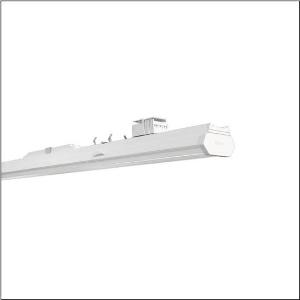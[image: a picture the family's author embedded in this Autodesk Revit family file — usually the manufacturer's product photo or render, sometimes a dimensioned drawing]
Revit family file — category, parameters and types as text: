
# Revit family: licross_11_protected_mo_51tp12dn695g
name_source: partatom
category: Lighting Fixtures
units: mm (PartAtom-declared; Revit-internal decimal feet)

## family parameters
Cut with Voids When Loaded = No
Host = Face
Light Source = No
Part Type = Normal
Room Calculation Point = No
Round Connector Dimension = Use Diameter
Shared = No

## types (1)
- --- (1 x LED, 9730 lm, 57.1 W, 6500K)
    Apparent Load = 57 VA
    CIE Flux Codes = 73 92 98 99 100
    Color Rendering = 80
    Color Temperature = 6500K
    Default Elevation = 1800 mm
    Description = Licross 11 Protected MO, luminaire insert, of sheet steel, galvanised, coil coated, white, length: 1.500mm, width: 90mm, height: 101mm, LED rated luminous flux: 9.730lm, light colour: 865, SDCM (Standard Deviation of Colour Matching)MacAdam ≤ 2 SDCM (initial), control gear: DALI 2, with plug, 5-pole, with phase selection, mains connection: 220..240V, AC, 50/60Hz, rated input power: 57W, internal wiring halogen-free, primary optical cover: cover, of PMMA, light emission: direct distribution, primary light characteristic: symmetric, protection rating (complete): IP64, insulation class (complete): insulation class I (protective earthing), certification: CE, ENEC, VDE, UKCA, protection symbol: D if used in an environment with conductive dust loads with corresponding accessories, impact resistance: IK06, permissible ambient temperature for indoor applications: -25..+35°C, corresponds to IFS (International Featured Standards) requirements for safety and quality in the food industry, reducing of maximum allowable ambient temperature of 5°C with ceiling mounting, LABS conformity tested according to VDMA 24364:2018-05, The light source and the operating device comply with the requirements of the Ecodesign Regulation (EU) 2019/2020 and are replaceable in accordance with this regulation, packaging unit: 1 piece
    Height = 92 mm
    Lamp = 1 x LED
    Lamp Light Flux = 9730 lm
    Lamp Power = 57.1 W
    Lamp count = 1
    Length = 1500 mm
    Luminous efficacy = 170 lm/W
    Manufacturer = Siteco
    ModVariant = No
    Model = 51TP12DN695G
    Mounting Place = Ceiling
    Mounting Type = Pendant
    Number of Poles = 1
    OnlyDefault = Yes
    Power Factor = 1
    Product Name = Licross 11 Protected MO
    Product group = luminaire insert | ceiling pendant
    ProductGroupID = 901
    Protection Class = Protection class I
    Protection Degree = IP 64
    RLX_Detail_Level = 1
    RLX_Emergency_Light_Flux = 0 lm
    RLX_Emergency_Type = 0
    RLX_Emergency_Type_DB = No
    RlxData = <blob elided: 24609 chars, md5=ad9be9ac>
    Socket = socket
    Standby Power = 0 W
    System Light Flux = 9730 lm
    System Power = 57 W
    Type Comments = factory setting: luminous flux: 100 % | dim-lin: 254 | 378 mA
    Type Image = l_1256148.jpg
    URL = http://relux.com
    VarID = @adj_086859
    Voltage = 0 V
    Weight = 0.00 kg
    Width = 88 mm

## geometry (parser evidence)
native form markers: Blend x4, Sweep x12
no freeform markers — native parametric forms only
